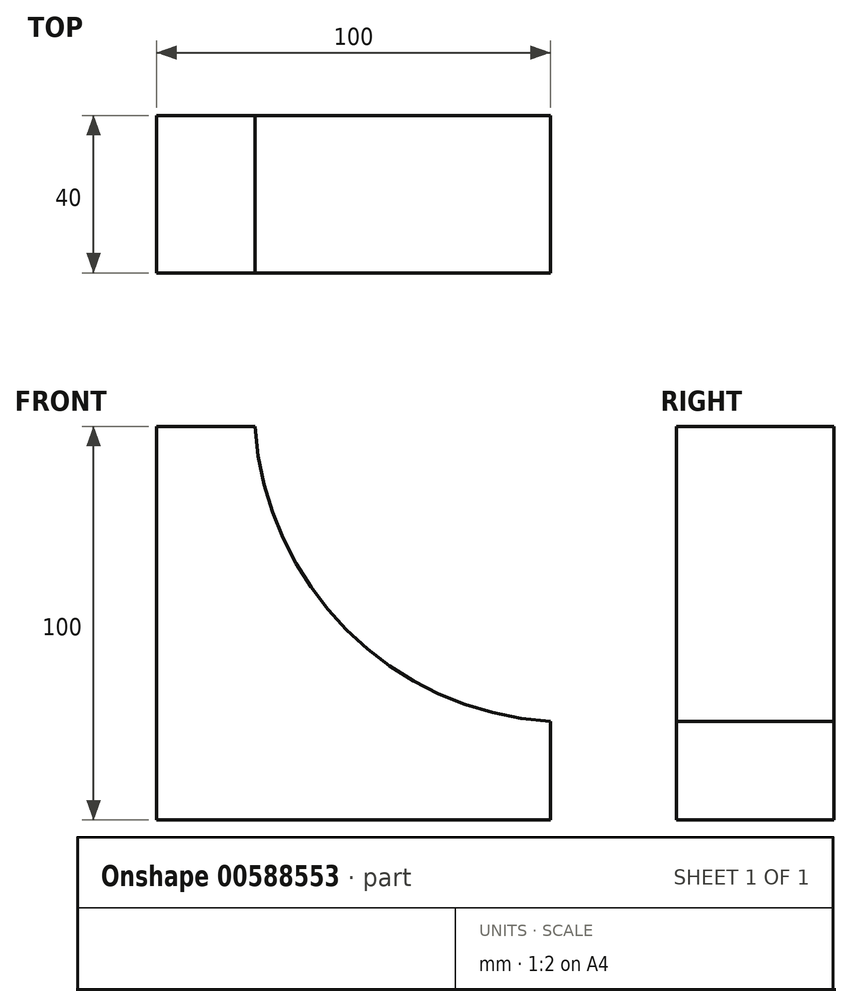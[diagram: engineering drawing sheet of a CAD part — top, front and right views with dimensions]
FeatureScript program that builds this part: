
annotation { "Feature Type Name" : "Feature", "Feature Type Description" : "" }
export const myFeature = defineFeature(function(context is Context, id is Id, definition is map)
    precondition{}
    {
        {
            var Q0;
            Q0=qCreatedBy(makeId("Front.planeOp"),FACE);
            var sketch = newSketch(context, id + "F0", { "sketchPlane" : qUnion([Q0])});
            skLineSegment(sketch, "E0", {"start": v(25, 100) * mm, "end": v(0, 100) * mm});
            skLineSegment(sketch, "E1", {"start": v(0, 100) * mm, "end": v(0, 0) * mm});
            skLineSegment(sketch, "E2", {"start": v(0, 0) * mm, "end": v(100, 0) * mm});
            skLineSegment(sketch, "E3", {"start": v(100, 0) * mm, "end": v(100, 25) * mm});
            skArc(sketch, "E4", {"start": v(25, 100) * mm, "mid": v(48.28, 48.28) * mm, "end": v(100, 25) * mm});
            skSolve(sketch);
        }
        {
            var Q0;
            Q0=makeQuery(id+"F0.imprint","IMPRINT",FACE,{"disambiguationData":[TD([[makeQuery(id+"F0.imprint","IMPRINT",EDGE,{"derivedFrom":sQuery(id+"F0.wireOp",EDGE,"E0")}),1.0]])]});
            extrude(context, id + "F1", {"entities" : qUnion([Q0]), "depth" : 40 * mm, "offsetDistance" : 25 * mm});
        }
    });
